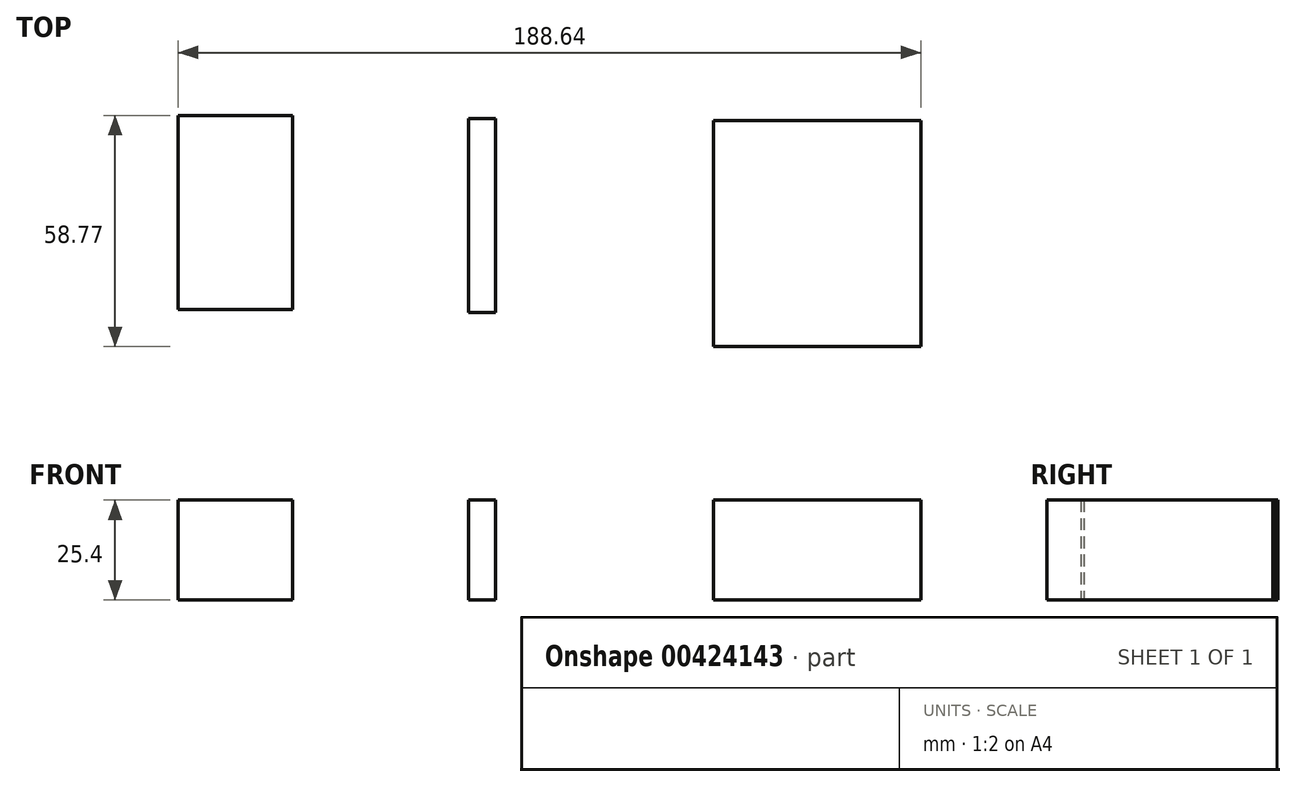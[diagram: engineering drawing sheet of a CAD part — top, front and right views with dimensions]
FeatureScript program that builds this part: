
annotation { "Feature Type Name" : "Feature", "Feature Type Description" : "" }
export const myFeature = defineFeature(function(context is Context, id is Id, definition is map)
    precondition{}
    {
        {
            var Q0;
            Q0=qCreatedBy(makeId("Top.planeOp"),FACE);
            var sketch = newSketch(context, id + "F0", { "sketchPlane" : qUnion([Q0])});
            skLineSegment(sketch, "E0.bottom", {"start": v(-59.15, 12.51) * mm, "end": v(-30.15, 12.51) * mm});
            skLineSegment(sketch, "E0.top", {"start": v(-59.15, -36.78) * mm, "end": v(-30.15, -36.78) * mm});
            skLineSegment(sketch, "E0.left", {"start": v(-59.15, 12.51) * mm, "end": v(-59.15, -36.78) * mm});
            skLineSegment(sketch, "E0.right", {"start": v(-30.15, 12.51) * mm, "end": v(-30.15, -36.78) * mm});
            skLineSegment(sketch, "E1.bottom", {"start": v(14.6, 11.76) * mm, "end": v(21.42, 11.76) * mm});
            skLineSegment(sketch, "E1.top", {"start": v(14.6, -37.54) * mm, "end": v(21.42, -37.54) * mm});
            skLineSegment(sketch, "E1.left", {"start": v(14.6, 11.76) * mm, "end": v(14.6, -37.54) * mm});
            skLineSegment(sketch, "E1.right", {"start": v(21.42, 11.76) * mm, "end": v(21.42, -37.54) * mm});
            skLineSegment(sketch, "E2.bottom", {"start": v(76.79, 11.19) * mm, "end": v(129.5, 11.19) * mm});
            skLineSegment(sketch, "E2.top", {"start": v(76.79, -46.26) * mm, "end": v(129.5, -46.26) * mm});
            skLineSegment(sketch, "E2.left", {"start": v(76.79, 11.19) * mm, "end": v(76.79, -46.26) * mm});
            skLineSegment(sketch, "E2.right", {"start": v(129.5, 11.19) * mm, "end": v(129.5, -46.26) * mm});
            skSolve(sketch);
        }
        {
            var Q0;
            Q0=makeQuery(id+"F0.imprint","IMPRINT",FACE,{"disambiguationData":[TD([[makeQuery(id+"F0.imprint","IMPRINT",EDGE,{"derivedFrom":sQuery(id+"F0.wireOp",EDGE,"E0.bottom")}),-1.0]])]});
            var Q1;
            Q1=makeQuery(id+"F0.imprint","IMPRINT",FACE,{"disambiguationData":[TD([[makeQuery(id+"F0.imprint","IMPRINT",EDGE,{"derivedFrom":sQuery(id+"F0.wireOp",EDGE,"E1.bottom")}),-1.0]])]});
            var Q2;
            Q2=makeQuery(id+"F0.imprint","IMPRINT",FACE,{"disambiguationData":[TD([[makeQuery(id+"F0.imprint","IMPRINT",EDGE,{"derivedFrom":sQuery(id+"F0.wireOp",EDGE,"E2.bottom")}),-1.0]])]});
            extrude(context, id + "F1", {"entities" : qUnion([Q0, Q1, Q2]), "depth" : 25.4 * mm});
        }
    });
